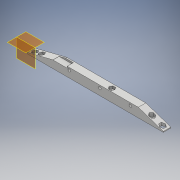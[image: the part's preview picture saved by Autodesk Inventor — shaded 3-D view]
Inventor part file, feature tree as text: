
AUTODESK INVENTOR PART (.ipt)
format: ipt  version: 2019 (Build 230136000, 136)  size: 252,928 bytes
history: native  units: mm
features: extrude x11, sketch x10, plane x7
ambient origin geometry x8: Origin, YZ Plane, XZ Plane, XY Plane, X Axis, Y Axis, Z Axis, Center Point
bodies: Solid1 (feature_tree)
feature tree (28):
  sketch  "Sketch1"  dims[d1=9.0mm d2=90.0deg]
  plane  "Work Plane2"
  sketch  "Sketch2"  dims[d6=3.2mm d7=3.2mm]
  plane  "Work Plane1"
  extrude  "klocek"  TaperAngle=90.0deg  [1 undecoded]
  plane  "Work Plane3"
  extrude  "prowadzenie osi"  Depth=3.2mm
  plane  "Work Plane4"
  sketch  "Sketch7"  dims[d15=3.2mm d17=3.2mm]
  sketch  "Sketch8"  dims[d18=36.5mm d26=3.2mm]
  extrude  "przedni skos"  Depth=3.2mm
  extrude  "tylni skos"  Depth=3.2mm
  plane  "Work Plane7"
  sketch  "Sketch5"  dims[d9=60.5mm d13=3.2mm]
  extrude  "hex insert middle"  Depth=3.2mm
  plane  "Work Plane6"
  sketch  "Sketch9"  dims[d27=48.0mm d28=3.2mm]
  extrude  "hex insert rear 1"  Depth=3.2mm
  plane  "Work Plane5"
  extrude  "hex insert rear 2"  Depth=5.0mm
  extrude  "hex insert front 1"  TaperAngle=0.0deg  [1 undecoded]
  extrude  "hex insert front 2"  Depth=8.0mm
  extrude  "ciecie przod"  Depth=5.9mm
  extrude  "sensor linii"  Depth=5.9mm
  sketch  "Sketch10"  dims[d32=15.0mm d33=5.0mm]
  sketch  "Sketch16"  dims[d38=11.0mm d39=0.0mm]
  sketch  "Sketch17"  dims[d61=3.2mm d62=8.0mm]
  sketch  "Sketch18"  dims[d63=12.5mm d64=52.0mm d65=36.5mm d67=11.0mm d68=0.0mm d70=7.5mm d71=0.0mm d77=5.0mm d78=0.0mm d80=10.0mm d81=30.0mm d82=3.0mm d83=0.0mm d84=8.5mm d85=0.0mm d86=10.0mm d87=40.0mm d88=7.0mm d89=0.0mm d91=9.0mm d92=0.0mm d93=5.9mm d94=9.0mm d95=0.0mm d96=10.0mm d97=0.0mm d98=5.9mm d99=5.9mm d102=2.0mm d103=17.0mm d104=2.5mm d105=7.3mm d106=0.0mm d108=4.0mm d109=4.0mm d111=4.0mm d112=4.0mm d113=4.0mm d114=8.0mm d115=73.0mm d118=5.9mm d122=2.0mm d123=5.9mm]
note: 2 required parameter values undecoded (feature->parameter linkage not recoverable at this tier; creation-order binding heuristic only, values carry confidence <= 0.55)
